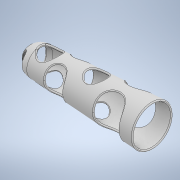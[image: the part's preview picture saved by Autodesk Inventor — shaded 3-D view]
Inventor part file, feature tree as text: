
AUTODESK INVENTOR PART (.ipt)
format: ipt  version: 2020 (Build 240168000, 168)  size: 806,400 bytes
history: native  units: in
note: dims shown in document units (in); Inventor stores cm internally (conversion verified against a paired STEP export)
features: sketch x2, revolve x1, extrude x1, fillet x1
ambient origin geometry x8: Origin, YZ Plane, XZ Plane, XY Plane, X Axis, Y Axis, Z Axis, Center Point
bodies: Solid1 (feature_tree)
feature tree (5):
  revolve  "Revolution1"  [1 undecoded]
  extrude  "Extrusion1"  Depth=0.0197in
  fillet  "Fillet1"  Radius=0.0394in
  sketch  "Sketch1"  dims[d0=0.5906in d1=2.3622in]
  sketch  "Sketch2"  dims[d2=0.4331in d3=0.0394in d4=0.0394in d5=360.0deg d6=0.1575in d7=0.1575in d8=0.1575in d9=0.3937in d10=0.315in d11=1.0in d12=0.0in d13=0.0197in d14=0.0344in]
note: 1 required parameter value undecoded (feature->parameter linkage not recoverable at this tier; creation-order binding heuristic only, values carry confidence <= 0.55)
